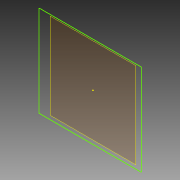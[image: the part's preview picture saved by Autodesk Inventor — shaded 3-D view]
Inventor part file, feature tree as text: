
AUTODESK INVENTOR PART (.ipt)
format: ipt  version: 2013 (Build 170138000, 138)  size: 58,368 bytes
history: native  units: in
note: dims shown in document units (in); Inventor stores cm internally (conversion verified against a paired STEP export)
features: plane x1, sketch x1
ambient origin geometry x8: Origin, YZ Plane, XZ Plane, XY Plane, X Axis, Y Axis, Z Axis, Center Point
feature tree (2):
  plane  "Work Plane1"
  sketch  "Sketch1"
